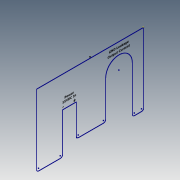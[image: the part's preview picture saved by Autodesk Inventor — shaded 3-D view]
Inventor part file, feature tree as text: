
AUTODESK INVENTOR PART (.ipt)
format: ipt  version: 2020.5 (Build 245400000, 400)  size: 134,656 bytes
history: native  units: mm
features: sketch x1
ambient origin geometry x8: Origin, YZ Plane, XZ Plane, XY Plane, X Axis, Y Axis, Z Axis, Center Point
feature tree (1):
  sketch  "Sketch30"  dims[d13=18.0mm d14=60.0mm d660=18.6mm d661=2.7mm d662=2.7mm d663=21.1mm d664=17.761013mm d665=4.351086mm d666=16.511013mm d667=8.051086mm d668=2.1mm d669=2.1mm d670=8.9mm d671=13.1mm d672=2.6mm d673=3.3mm d674=1.8mm d675=0.6mm d676=23.909893mm d677=26.009893mm d678=20.194718mm d679=23.294718mm d680=26.905472mm d681=27.908194mm d682=16.158484mm d683=26.020802mm]
